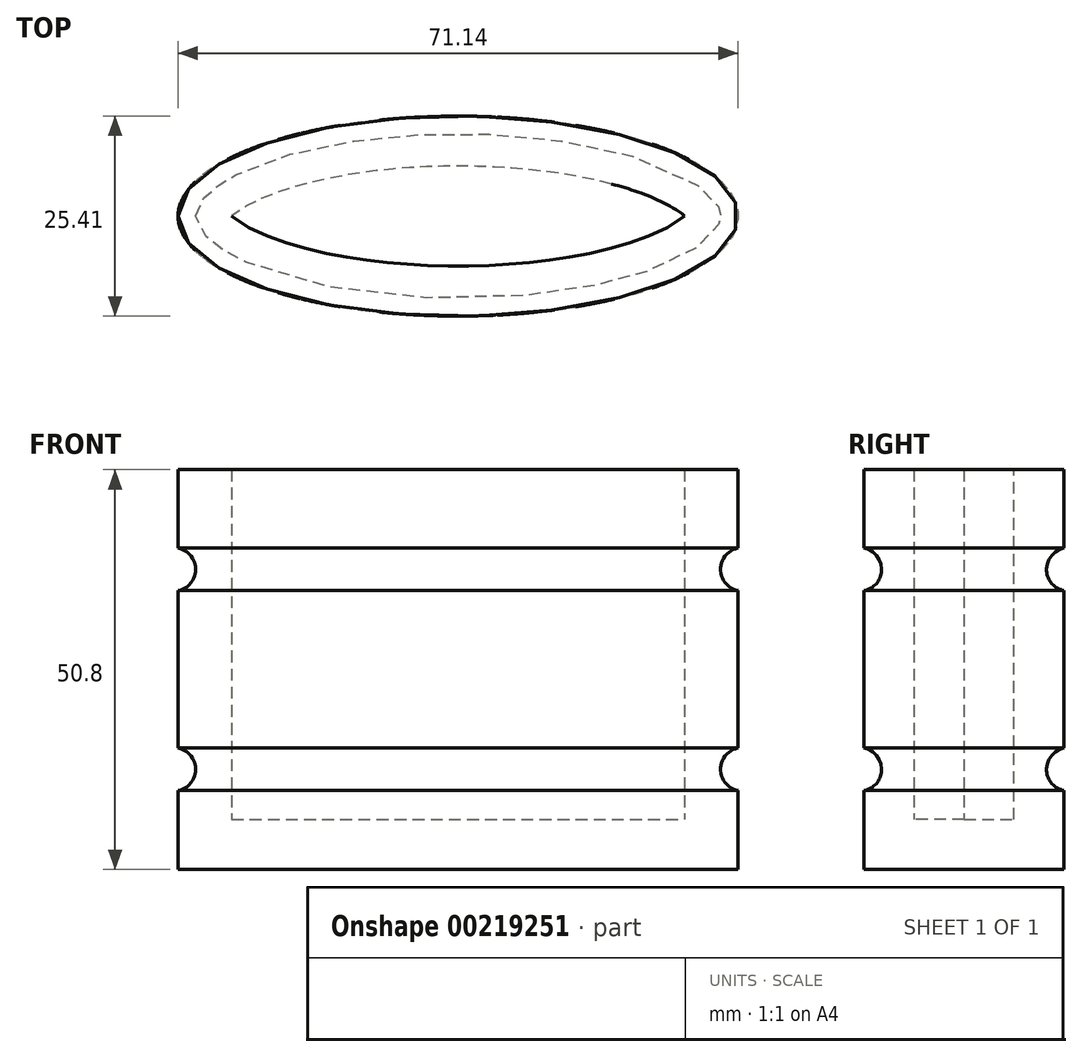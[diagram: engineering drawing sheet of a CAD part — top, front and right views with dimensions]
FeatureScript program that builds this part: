
annotation { "Feature Type Name" : "Feature", "Feature Type Description" : "" }
export const myFeature = defineFeature(function(context is Context, id is Id, definition is map)
    precondition{}
    {
        {
            var Q0;
            Q0=qCreatedBy(makeId("Front.planeOp"),FACE);
            var sketch = newSketch(context, id + "F0", { "sketchPlane" : qUnion([Q0])});
            skEllipse(sketch, "E0", {"center": v(0, 0) * mm, "majorRadius": 35.57 * mm, "minorRadius": 12.7 * mm, "majorAxis": v(-1, 0)});
            skSolve(sketch);
        }
        {
            var Q0;
            Q0 = qSketchRegion(id + "F0", true);
            extrude(context, id + "F1", {"entities" : qUnion([Q0]), "depth" : 50.8 * mm});
        }
        {
            var Q0;
            Q0=qCreatedBy(makeId("Top.planeOp"),FACE);
            var sketch = newSketch(context, id + "F2", { "sketchPlane" : qUnion([Q0])});
            skLineSegment(sketch, "E1", {"start": v(-36.9, -24.6) * mm, "end": v(39.3, -24.6) * mm});
            skLineSegment(sketch, "E2", {"start": v(-39, -34.74) * mm, "end": v(44.52, -34.74) * mm});
            skSolve(sketch);
        }
        {
            var Q0;
            Q0=makeQuery(id+"F1.opExtrude","CAP_FACE",FACE,{"disambiguationData":[OSD([sQuery(id+"F0.wireOp",EDGE,"E0")])],"isStart":false});
            shell(context, id + "F3", {"entities" : qUnion([Q0]), "thickness" : 6.35 * mm});
        }
        {
            var Q0;
            Q0=qCreatedBy(makeId("Right.planeOp"),FACE);
            var sketch = newSketch(context, id + "F4", { "sketchPlane" : qUnion([Q0])});
            skCircle(sketch, "E3", {"center": v(-38.12, -13.23) * mm, "radius": 2.75 * mm});
            skCircle(sketch, "E4.1.0.0", {"center": v(-12.72, -13.23) * mm, "radius": 2.75 * mm});
            skCircle(sketch, "E4.2.0.0", {"center": v(12.68, -13.23) * mm, "radius": 2.75 * mm});
            skLineSegment(sketch, "E4.direction1", {"start": v(-38.12, -13.23) * mm, "end": v(-12.72, -13.23) * mm, "construction": true});
            skSolve(sketch);
        }
        {
            var Q0;
            Q0 = qSketchRegion(id + "F4", true);
            var Q1;
            Q1=makeQuery(id+"F1.opExtrude","CAP_EDGE",EDGE,{"disambiguationData":[OSD([sQuery(id+"F0.wireOp",EDGE,"E0")])],"isStart":true});
            sweep(context, id + "F5", {"operationType" : NewBodyOperationType.REMOVE, "profiles" : qUnion([Q0]), "path" : qUnion([Q1])});
        }
        {
            var Q0;
            Q0=makeQuery(id+"F1.opExtrude","SWEPT_BODY",BODY,{"disambiguationData":[OSD([sQuery(id+"F0.wireOp",EDGE,"E0")])]});
            var Q1;
            Q1=sQuery(id+"F2.wireOp",EDGE,"E2");
            transform(context, id + "F6", {"entities" : qUnion([Q0]), "transformType" : TransformType.ROTATION, "transformAxis" : qUnion([Q1]), "angle" : 90 * degree, "oppositeDirection" : true, "makeCopy" : false});
        }
    });
